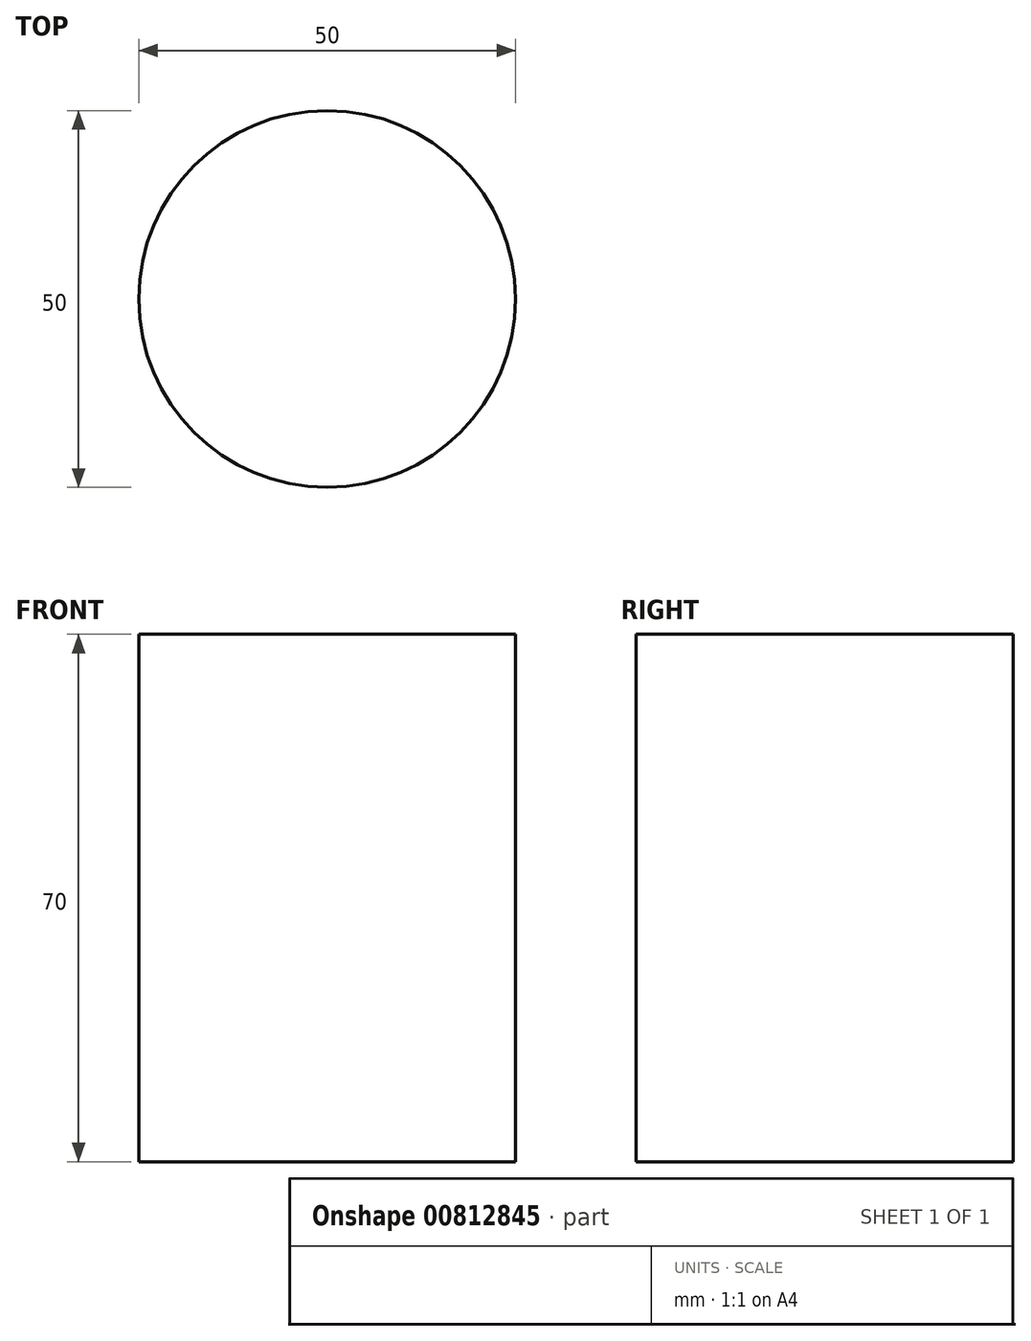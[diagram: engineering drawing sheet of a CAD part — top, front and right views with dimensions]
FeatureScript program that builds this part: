
annotation { "Feature Type Name" : "Feature", "Feature Type Description" : "" }
export const myFeature = defineFeature(function(context is Context, id is Id, definition is map)
    precondition{}
    {
        {
            var Q0;
            Q0=qCreatedBy(makeId("Top.planeOp"),FACE);
            var sketch = newSketch(context, id + "F0", { "sketchPlane" : qUnion([Q0])});
            skCircle(sketch, "E0", {"center": v(0, -3.44) * mm, "radius": 25 * mm});
            skSolve(sketch);
        }
        {
            var Q0;
            Q0=makeQuery(id+"F0.imprint","IMPRINT",FACE,{"disambiguationData":[TD([[makeQuery(id+"F0.imprint","IMPRINT",EDGE,{"derivedFrom":sQuery(id+"F0.wireOp",EDGE,"E0")}),1.0]])]});
            var Q1;
            Q1=sQuery(id+"F0.wireOp",EDGE,"E0");
            extrude(context, id + "F1", {"entities" : qUnion([Q0]), "surfaceEntities" : qUnion([Q1]), "depth" : 70 * mm, "offsetDistance" : 25 * mm});
        }
    });
